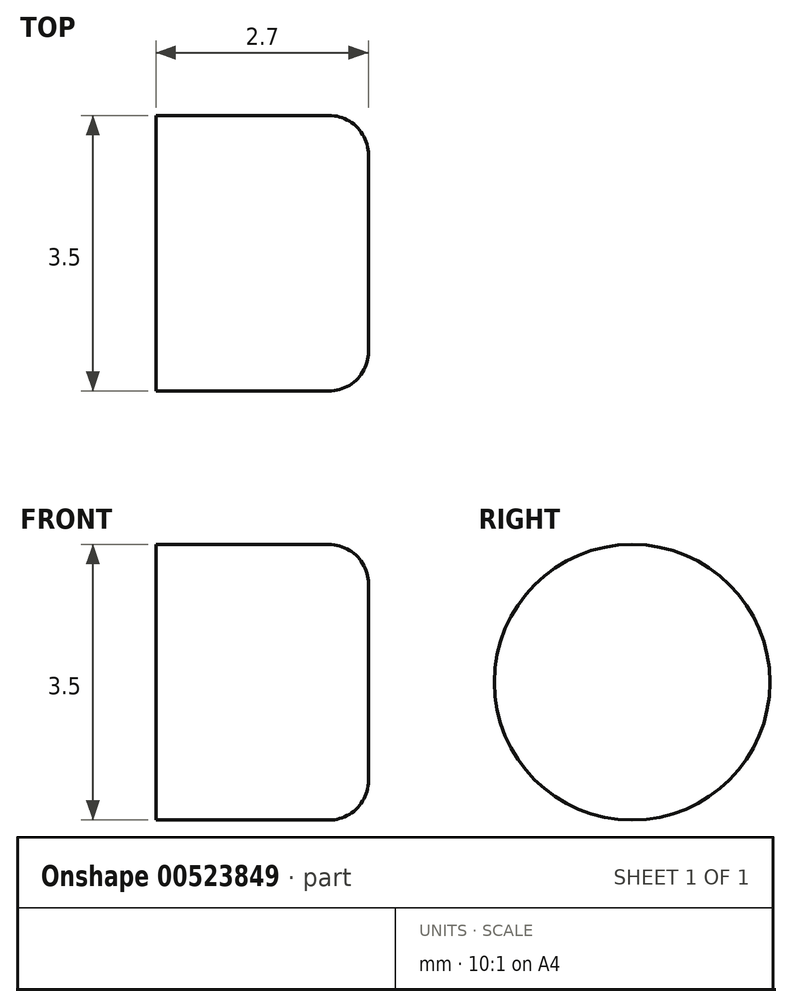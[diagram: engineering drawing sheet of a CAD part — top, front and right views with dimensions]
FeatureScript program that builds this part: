
annotation { "Feature Type Name" : "Feature", "Feature Type Description" : "" }
export const myFeature = defineFeature(function(context is Context, id is Id, definition is map)
    precondition{}
    {
        {
            var Q0;
            Q0=qCreatedBy(makeId("Right.planeOp"),FACE);
            var sketch = newSketch(context, id + "F0", { "sketchPlane" : qUnion([Q0])});
            skCircle(sketch, "E0", {"center": v(0, 0) * mm, "radius": 1.75 * mm});
            skSolve(sketch);
        }
        {
            var Q0;
            Q0=makeQuery(id+"F0.imprint","IMPRINT",FACE,{"disambiguationData":[TD([[makeQuery(id+"F0.imprint","IMPRINT",EDGE,{"derivedFrom":sQuery(id+"F0.wireOp",EDGE,"E0")}),1.0]])]});
            extrude(context, id + "F1", {"entities" : qUnion([Q0]), "endBound" : BoundingType.SYMMETRIC, "depth" : 2.7 * mm, "offsetDistance" : 25 * mm});
        }
        {
            var Q0;
            Q0=makeQuery(id+"F1.opExtrude","CAP_FACE",FACE,{"disambiguationData":[OSD([sQuery(id+"F0.wireOp",EDGE,"E0")])],"isStart":false});
            fillet(context, id + "F2", {"entities" : qUnion([Q0]), "radius" : 0.5 * mm, "tangentPropagation" : true, "allowEdgeOverflow" : false});
        }
    });
